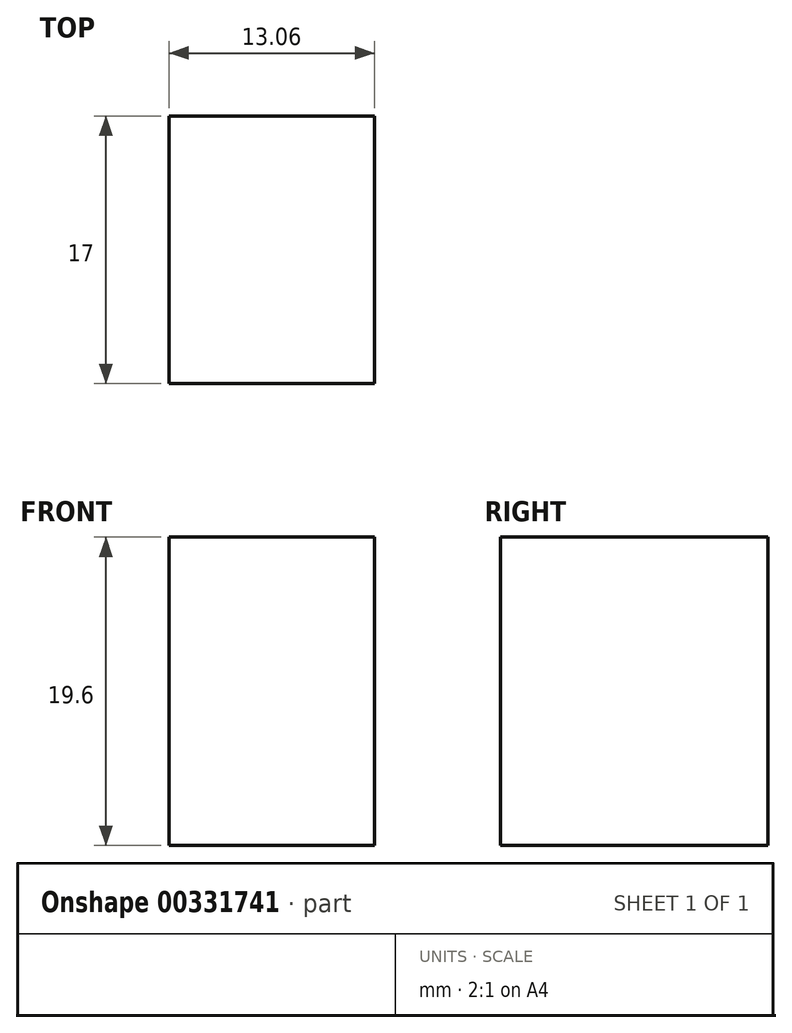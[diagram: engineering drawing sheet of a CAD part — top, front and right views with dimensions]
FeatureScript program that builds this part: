
annotation { "Feature Type Name" : "Feature", "Feature Type Description" : "" }
export const myFeature = defineFeature(function(context is Context, id is Id, definition is map)
    precondition{}
    {
        {
            var Q0;
            Q0=qCreatedBy(makeId("Front.planeOp"),FACE);
            var sketch = newSketch(context, id + "F0", { "sketchPlane" : qUnion([Q0])});
            skLineSegment(sketch, "E0.bottom", {"start": v(-6.53, -9.8) * mm, "end": v(6.53, -9.8) * mm});
            skLineSegment(sketch, "E0.top", {"start": v(-6.53, 9.8) * mm, "end": v(6.53, 9.8) * mm});
            skLineSegment(sketch, "E0.left", {"start": v(-6.53, -9.8) * mm, "end": v(-6.53, 9.8) * mm});
            skLineSegment(sketch, "E0.right", {"start": v(6.53, -9.8) * mm, "end": v(6.53, 9.8) * mm});
            skPoint(sketch, "E0.middle", {"position": v(0, 0) * mm});
            skSolve(sketch);
        }
        {
            var Q0;
            Q0=qSketchRegion(id+"F0",true);
            extrude(context, id + "F1", {"entities" : qUnion([Q0]), "depth" : 17 * mm});
        }
    });
